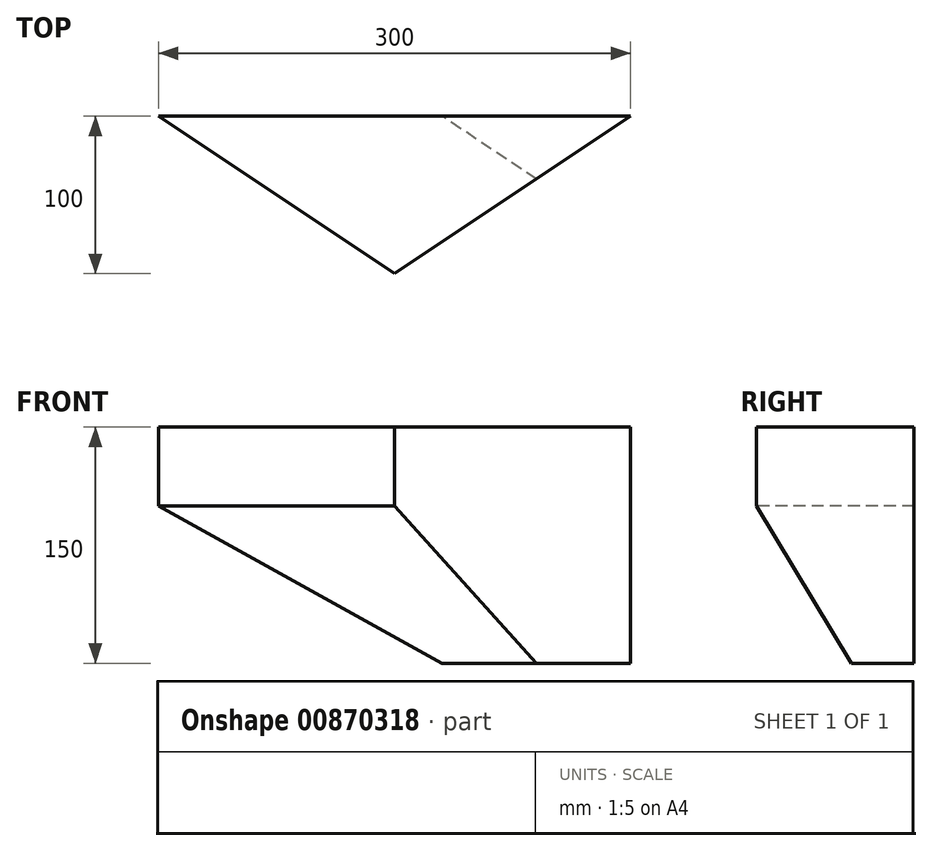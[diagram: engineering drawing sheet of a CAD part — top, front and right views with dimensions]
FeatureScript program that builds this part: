
annotation { "Feature Type Name" : "Feature", "Feature Type Description" : "" }
export const myFeature = defineFeature(function(context is Context, id is Id, definition is map)
    precondition{}
    {
        {
            var Q0;
            Q0=qCreatedBy(makeId("Top.planeOp"),FACE);
            var sketch = newSketch(context, id + "F0", { "sketchPlane" : qUnion([Q0])});
            skLineSegment(sketch, "E0.top", {"start": v(0, 100) * mm, "end": v(-150, 100) * mm});
            skLineSegment(sketch, "E1.top", {"start": v(0, 100) * mm, "end": v(150, 100) * mm});
            skLineSegment(sketch, "E2", {"start": v(0, 0) * mm, "end": v(150, 100) * mm});
            skLineSegment(sketch, "E3", {"start": v(0, 0) * mm, "end": v(-150, 100) * mm});
            skSolve(sketch);
        }
        {
            var Q0;
            Q0 = qSketchRegion(id + "F0", true);
            extrude(context, id + "F1", {"entities" : qUnion([Q0]), "endBound" : BoundingType.SYMMETRIC, "depth" : 150 * mm, "offsetDistance" : 25 * mm});
        }
        {
            var Q0;
            Q0=makeQuery(id+"F1.opExtrude","CAP_EDGE",EDGE,{"disambiguationData":[OSD([sQuery(id+"F0.wireOp",EDGE,"E3")])],"isStart":true});
            chamfer(context, id + "F2", {"entities" : qUnion([Q0]), "width" : 100 * mm, "tangentPropagation" : true});
        }
    });
